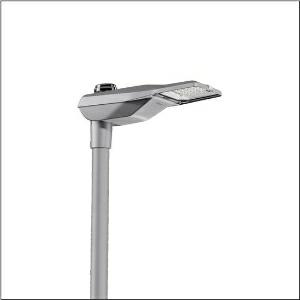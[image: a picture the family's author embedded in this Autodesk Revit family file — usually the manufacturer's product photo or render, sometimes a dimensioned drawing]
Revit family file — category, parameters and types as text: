
# Revit family: streetlight_sl_21_micro___stw1_0a_5xe5e37n08cb_b20b
name_source: partatom
category: Lighting Fixtures
units: mm (PartAtom-declared; Revit-internal decimal feet)

## family parameters
Cut with Voids When Loaded = No
Host = Face
Light Source = No
Part Type = Normal
Room Calculation Point = No
Round Connector Dimension = Use Diameter
Shared = No

## types (1)
- --- (1 x LED, 2290 lm, 15.8 W, 3000K)
    Apparent Load = 16 VA
    CIE Flux Codes = 38 75 98 100 100
    Color Rendering = 70
    Color Temperature = 3000K
    Default Elevation = 1800 mm
    Description = Streetlight SL 21 micro, mast luminaire, primary light control with lens, of PMMA, primary optical cover: cover, of toughened safety glass, transparent, light distribution: STW1.0a, light emission: direct distribution, primary light characteristic: asymmetric, installation type: post-top, LED, 3G 1.5mm², High Power LED, rated luminous flux: 2.290lm, luminous efficacy: 145lm/W, light colour: 730, colour temperature: 3000K, control gear: NEMA (7pin), control: overheat protection, pre-setting: linear dimming characteristic, constant luminous flux control, time-dependent luminous flux control, flexible luminous flux parameterisation, mains connection: 230..240V, AC, 50/60Hz, connection cable pre-assembled, cable length: 6,5m, wiring characteristics: H07RN-F, start of lifetime: 16W, end of service life: 16W, reduction: 8W, luminaire housing, of diecast aluminium (EN AC-44300), powder-coated, SITECO metallic grey (DB 702S), corrosivity category C5 high according to DIN EN ISO 12944, multi-level sealing system, sealing non-destructively replaceable, inclination adjustable: 0°, 5°, 10°, 15°, length: 528mm, width: 235mm, height: 110mm, spigot size: 76/60mm (post-top), mounting height: 4..8m, protection rating (complete): IP66, insulation class (complete): insulation class I (protective earthing), certification: CE, ENEC, ENEC+, VDE, impact resistance: IK10, permissible operating ambient temperature for outdoor applications: -40..+50°C, standard-compliant lighting for roads and squares, packaging unit: 1 piece

Light Distribution: STW1.0a
    Height = 110 mm
    Lamp = 1 x LED
    Lamp Light Flux = 2290 lm
    Lamp Power = 15.8 W
    Lamp count = 1
    Length = 528 mm
    Luminous efficacy = 145 lm/W
    Manufacturer = Siteco
    ModVariant = No
    Model = 5XE5E37N08CB
    Number of Poles = 1
    OnlyDefault = Yes
    Power Factor = 1
    Product Name = Streetlight SL 21 micro | STW1.0a
    Product group = mast luminaire | pylon top
    ProductGroupID = 6100
    Protection Class = Protection class I
    Protection Degree = IP 66
    RLX_Detail_Level = 1
    RLX_Emergency_Light_Flux = 0 lm
    RLX_Emergency_Type = 0
    RLX_Emergency_Type_DB = No
    RlxData = <blob elided: 98445 chars, md5=beeb19ae>
    Socket = socket
    Standby Power = 0 W
    System Light Flux = 2290 lm
    System Power = 16 W
    Type Comments = factory setting: luminous flux: 100 % | dim-lin: 254 | 300 mA
    Type Image = l_1294375.jpg
    URL = http://relux.com
    VarID = @adj_135357
    Voltage = 0 V
    Weight = 0.00 kg
    Width = 235 mm

## geometry (parser evidence)
native form markers: Blend x4, Sweep x9
no freeform markers — native parametric forms only
